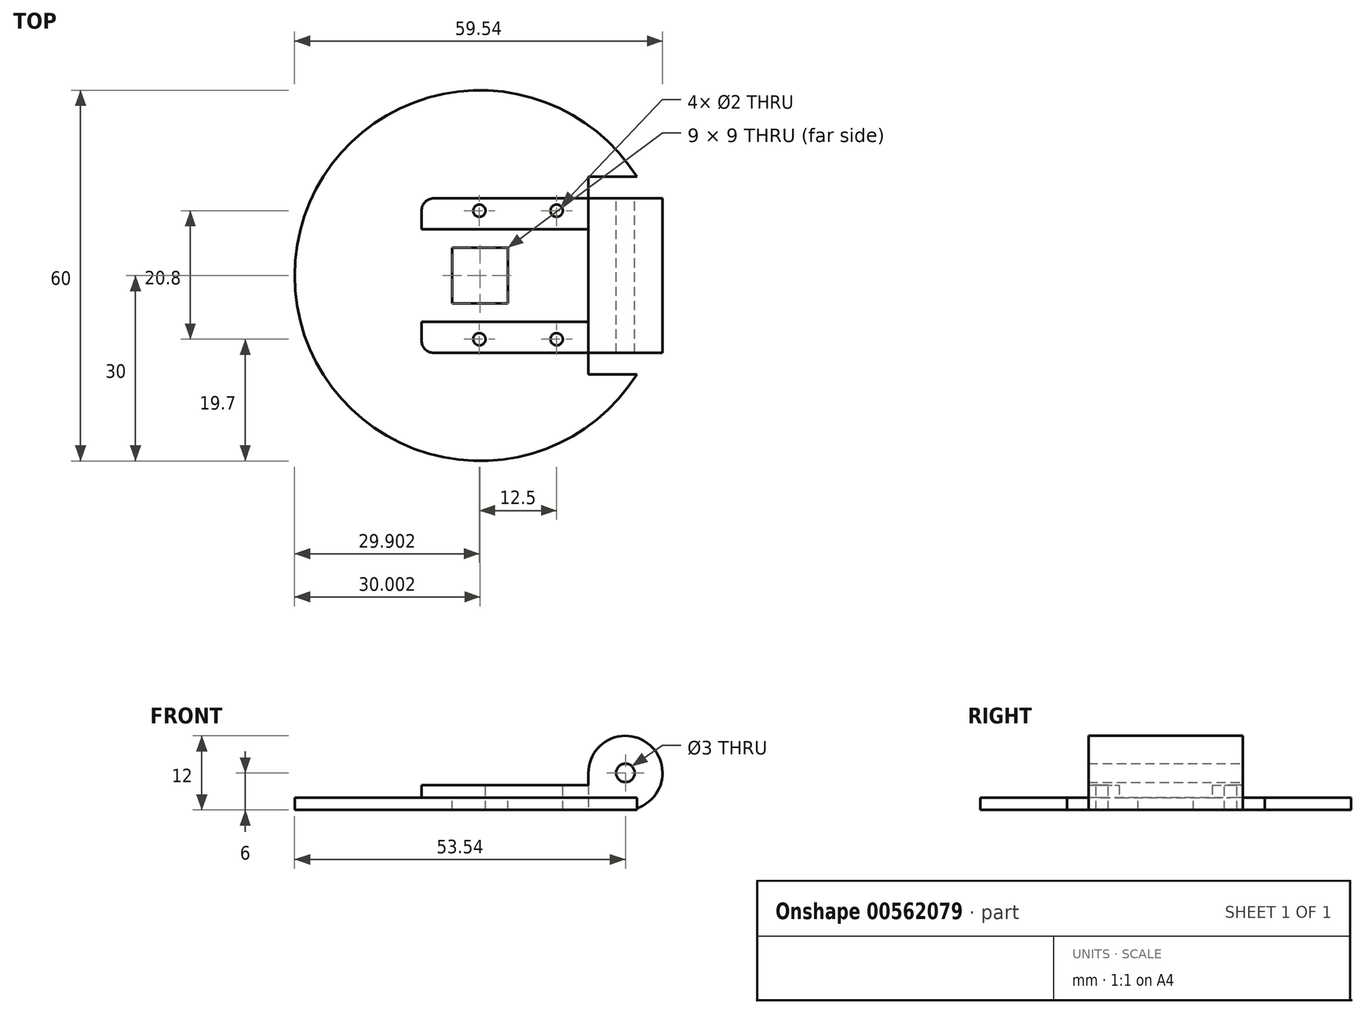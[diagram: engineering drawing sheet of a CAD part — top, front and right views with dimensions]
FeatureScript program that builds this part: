
annotation { "Feature Type Name" : "Feature", "Feature Type Description" : "" }
export const myFeature = defineFeature(function(context is Context, id is Id, definition is map)
    precondition{}
    {
        {
            var Q0;
            Q0=qCreatedBy(makeId("Front.planeOp"),FACE);
            var sketch = newSketch(context, id + "F0", { "sketchPlane" : qUnion([Q0])});
            skCircle(sketch, "E0", {"center": v(0, 0) * mm, "radius": 1.5 * mm});
            skArc(sketch, "E1", {"start": v(-6, 0) * mm, "mid": v(4.24, 4.24) * mm, "end": v(0, -6) * mm});
            skLineSegment(sketch, "E2", {"start": v(0, -6) * mm, "end": v(-33, -6) * mm});
            skLineSegment(sketch, "E3", {"start": v(-33, -6) * mm, "end": v(-33, -4) * mm});
            skLineSegment(sketch, "E4", {"start": v(-33, -4) * mm, "end": v(-6, -4) * mm});
            skLineSegment(sketch, "E5", {"start": v(-6, -4) * mm, "end": v(-6, 0) * mm});
            skSolve(sketch);
        }
        {
            var Q0;
            Q0=makeQuery(id+"F0.imprint","IMPRINT",FACE,{"disambiguationData":[TD([[makeQuery(id+"F0.imprint","IMPRINT",EDGE,{"derivedFrom":sQuery(id+"F0.wireOp",EDGE,"E0")}),-1.0]])]});
            extrude(context, id + "F1", {"entities" : qUnion([Q0]), "endBound" : BoundingType.SYMMETRIC, "depth" : 25 * mm, "offsetDistance" : 25 * mm});
        }
        {
            var Q0;
            Q0=makeQuery(id+"F1.opExtrude","CAP_EDGE",EDGE,{"disambiguationData":[OSD([sQuery(id+"F0.wireOp",EDGE,"E3")])],"isStart":false});
            var Q1;
            Q1=makeQuery(id+"F1.opExtrude","CAP_EDGE",EDGE,{"disambiguationData":[OSD([sQuery(id+"F0.wireOp",EDGE,"E3")])],"isStart":true});
            fillet(context, id + "F2", {"entities" : qUnion([Q0, Q1]), "radius" : 2 * mm, "tangentPropagation" : true, "allowEdgeOverflow" : false});
        }
        {
            var Q0;
            Q0=makeQuery(id+"F1.opExtrude","SWEPT_FACE",FACE,{"disambiguationData":[OSD([sQuery(id+"F0.wireOp",EDGE,"E4")])]});
            var sketch = newSketch(context, id + "F3", { "sketchPlane" : qUnion([Q0])});
            skLineSegment(sketch, "E6.bottom", {"start": v(-23.64, 10.5) * mm, "end": v(-11.14, 10.5) * mm, "construction": true});
            skLineSegment(sketch, "E6.top", {"start": v(-23.64, -10.3) * mm, "end": v(-11.14, -10.3) * mm, "construction": true});
            skLineSegment(sketch, "E6.left", {"start": v(-23.64, 10.5) * mm, "end": v(-23.64, -10.3) * mm, "construction": true});
            skLineSegment(sketch, "E6.right", {"start": v(-11.14, 10.5) * mm, "end": v(-11.14, -10.3) * mm, "construction": true});
            skLineSegment(sketch, "E7", {"start": v(-9.14, 12.5) * mm, "end": v(-9.14, -12.5) * mm, "construction": true});
            skCircle(sketch, "E8", {"center": v(-23.64, 10.5) * mm, "radius": 1 * mm});
            skCircle(sketch, "E9", {"center": v(-11.14, 10.5) * mm, "radius": 1 * mm});
            skCircle(sketch, "E10", {"center": v(-11.14, -10.3) * mm, "radius": 1 * mm});
            skCircle(sketch, "E11", {"center": v(-23.64, -10.3) * mm, "radius": 1 * mm});
            skLineSegment(sketch, "E12.bottom", {"start": v(-19.04, 4.5) * mm, "end": v(-28.04, 4.5) * mm});
            skLineSegment(sketch, "E12.top", {"start": v(-19.04, -4.5) * mm, "end": v(-28.04, -4.5) * mm});
            skLineSegment(sketch, "E12.left", {"start": v(-19.04, 4.5) * mm, "end": v(-19.04, -4.5) * mm});
            skLineSegment(sketch, "E12.right", {"start": v(-28.04, 4.5) * mm, "end": v(-28.04, -4.5) * mm});
            skPoint(sketch, "E12.middle", {"position": v(-23.54, 0) * mm});
            skSolve(sketch);
        }
        {
            var Q0;
            Q0 = qSketchRegion(id + "F3", true);
            extrude(context, id + "F4", {"entities" : qUnion([Q0]), "operationType" : NewBodyOperationType.REMOVE, "endBound" : BoundingType.UP_TO_NEXT, "oppositeDirection" : true, "depth" : 25 * mm, "offsetDistance" : 25 * mm});
        }
        {
            var Q0;
            Q0=makeQuery(id+"F1.opExtrude","SWEPT_FACE",FACE,{"disambiguationData":[OSD([sQuery(id+"F0.wireOp",EDGE,"E4")])]});
            var sketch = newSketch(context, id + "F5", { "sketchPlane" : qUnion([Q0])});
            skLineSegment(sketch, "E13", {"start": v(-6, 7.5) * mm, "end": v(-33, 7.5) * mm});
            skLineSegment(sketch, "E14", {"start": v(-6, -7.5) * mm, "end": v(-33, -7.5) * mm});
            skSolve(sketch);
        }
        {
            var Q0;
            {var subQ4=sQuery(id+"F5.wireOp",EDGE,"E14");Q0=makeQuery(id+"F5.imprint","IMPRINT",FACE,{"disambiguationData":[TD([[makeQuery(id+"F5.imprint","IMPRINT",EDGE,{"derivedFrom":subQ4}),1.0]])]});}
            var Q1;
            {var subQ4=sQuery(id+"F5.wireOp",EDGE,"E13");Q1=makeQuery(id+"F5.imprint","IMPRINT",FACE,{"disambiguationData":[TD([[makeQuery(id+"F5.imprint","IMPRINT",EDGE,{"derivedFrom":subQ4}),-1.0]])]});}
            extrude(context, id + "F6", {"entities" : qUnion([Q0, Q1]), "operationType" : NewBodyOperationType.ADD, "depth" : 2 * mm, "offsetDistance" : 25 * mm});
        }
        {
            var Q0;
            Q0=makeQuery(id+"F1.opExtrude","SWEPT_FACE",FACE,{"disambiguationData":[OSD([sQuery(id+"F0.wireOp",EDGE,"E2")])]});
            var sketch = newSketch(context, id + "F7", { "sketchPlane" : qUnion([Q0])});
            skArc(sketch, "E15", {"start": v(1.84, 16) * mm, "mid": v(-53.54, 0) * mm, "end": v(1.84, -16) * mm});
            skPoint(sketch, "E15.centerSnap0", {"position": v(-19.04, 0) * mm});
            skPoint(sketch, "E15.centerSnap1", {"position": v(-23.54, 4.5) * mm});
            skPoint(sketch, "E16.0", {"position": v(-6, 12.5) * mm});
            skPoint(sketch, "E17.0", {"position": v(-6, -12.5) * mm});
            skLineSegment(sketch, "E18", {"start": v(-6, 16) * mm, "end": v(1.84, 16) * mm});
            skLineSegment(sketch, "E19", {"start": v(-6, 16) * mm, "end": v(-6, 12.5) * mm});
            skLineSegment(sketch, "E20", {"start": v(-6, -12.5) * mm, "end": v(-6, -16) * mm});
            skLineSegment(sketch, "E21", {"start": v(-6, -16) * mm, "end": v(1.84, -16) * mm});
            skSolve(sketch);
        }
        {
            var Q0;
            Q0=makeQuery(id+"F7.imprint","IMPRINT",FACE,{"disambiguationData":[TD([[makeQuery(id+"F7.imprint","IMPRINT",EDGE,{"derivedFrom":sQuery(id+"F7.wireOp",EDGE,"E15")}),1.0]])]});
            var Q1;
            Q1=makeQuery(id+"F1.opExtrude","SWEPT_FACE",FACE,{"disambiguationData":[OSD([sQuery(id+"F0.wireOp",EDGE,"E4")])]});
            extrude(context, id + "F8", {"entities" : qUnion([Q0]), "operationType" : NewBodyOperationType.ADD, "endBound" : BoundingType.UP_TO_SURFACE, "oppositeDirection" : true, "depth" : 2 * mm, "endBoundEntityFace" : qUnion([Q1]), "offsetDistance" : 25 * mm});
        }
    });
